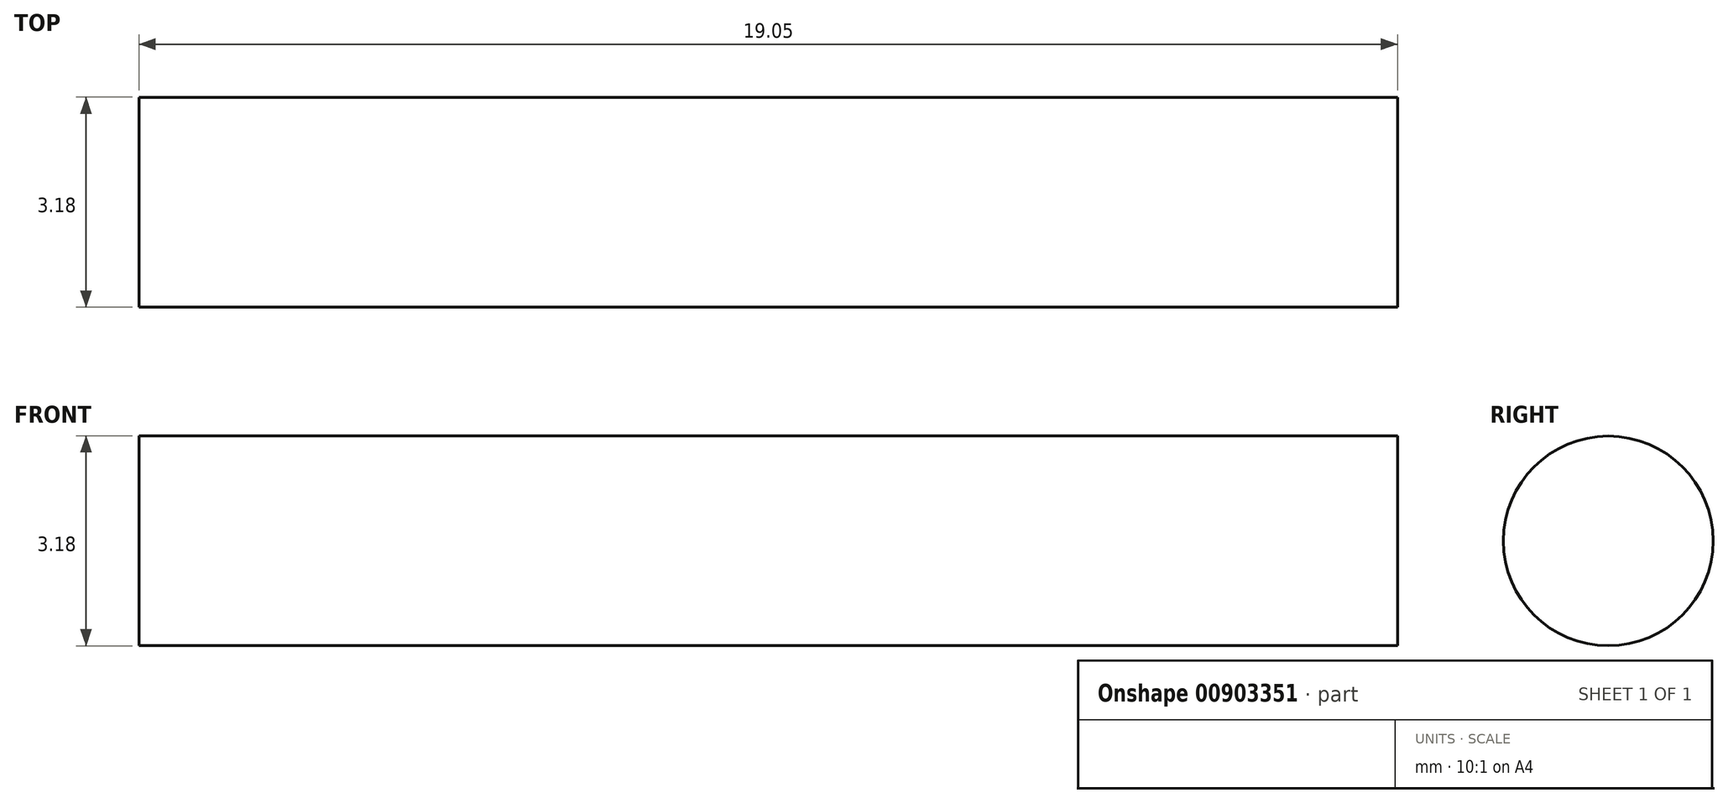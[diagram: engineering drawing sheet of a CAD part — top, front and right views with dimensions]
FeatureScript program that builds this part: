
annotation { "Feature Type Name" : "Feature", "Feature Type Description" : "" }
export const myFeature = defineFeature(function(context is Context, id is Id, definition is map)
    precondition{}
    {
        {
            var Q0;
            Q0=qCreatedBy(makeId("Right.planeOp"),FACE);
            var sketch = newSketch(context, id + "F0", { "sketchPlane" : qUnion([Q0])});
            skCircle(sketch, "E0", {"center": v(0, 0) * mm, "radius": 1.59 * mm});
            skSolve(sketch);
        }
        {
            var Q0;
            Q0 = qSketchRegion(id + "F0", true);
            extrude(context, id + "F1", {"entities" : qUnion([Q0]), "oppositeDirection" : true, "depth" : 19.05 * mm, "offsetDistance" : 25.4 * mm});
        }
    });
